# Revit family: Metal_Open_Access_Lockers-Salsbury_Industries-70000_Series
name_source: partatom
category: Specialty Equipment
revit_build: Autodesk Revit 2016 (Build: 20150714_1515(x64)
units: mm (PartAtom-declared; Revit-internal decimal feet)

## family parameters
Always vertical = Yes
Cut with Voids When Loaded = No
OmniClass Number = 23.40.00.00
OmniClass Title = Equipment and Furnishings
Part Type = Normal
Room Calculation Point = No
Round Connector Dimension = Use Diameter
Shared = No
Work Plane-Based = No

## types (2) — shared parameters
Assembly Code = C1030310
Hasp Handle Material = Plastic - Salsbury Finish - Black
Hasp Plate Rivet Material = Steel -Salsbury Finish - Polished Steel
Height = 72 "
Manufacturer = Salsbury Industries
MasterFormat Number = 10 51 13
MasterFormat Title = Lockers
OmniClass 23 Number = 23.40.00.00
OmniClass 23 Title = Equipment and Furnishings
Top Compartment Width = 12.02 "
Type Comments = 24" Wide Open Access Metal Locker
URL = www.lockers.com
Vent Array Spacing = 1.165 "
Vent Configuration Height = Vents : Open Access_Gear vents
Version = 1.0 (10/31/18)
Width = 24.04 "

## per-type parameters (varying)
| type | Depth | Description | Vent Array 1 | Vent Array 2 | Vent Offset |
| 70024 | 24.01 " | 6 Feet High - 24 Inches Deep | 13 | 14 | 4.375 " |
| 70018 | 18.01 " | 6 Feet High - 18 Inches Deep | 7 | 8 | 5 " |

note: column(s) folded — value = type name in every type: Model

## geometry (parser evidence)
native form markers: Sweep x9
no freeform markers — native parametric forms only
